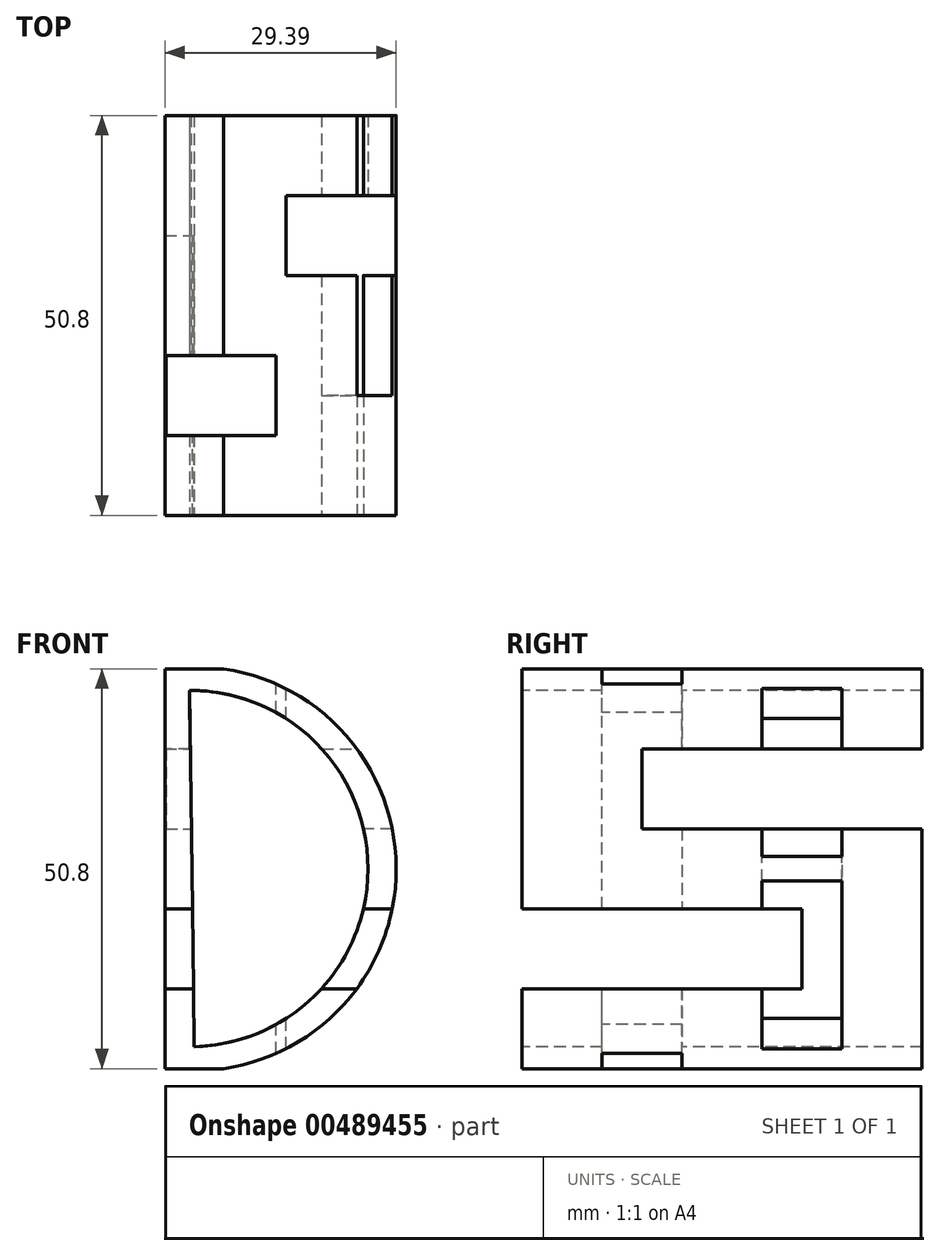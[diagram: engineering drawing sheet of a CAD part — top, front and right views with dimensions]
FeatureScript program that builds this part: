
annotation { "Feature Type Name" : "Feature", "Feature Type Description" : "" }
export const myFeature = defineFeature(function(context is Context, id is Id, definition is map)
    precondition{}
    {
        {
            var Q0;
            Q0=qCreatedBy(makeId("Front.planeOp"),FACE);
            var sketch = newSketch(context, id + "F0", { "sketchPlane" : qUnion([Q0])});
            skLineSegment(sketch, "E0", {"start": v(0, 0) * mm, "end": v(0, 50.8) * mm});
            skLineSegment(sketch, "E1", {"start": v(0, 50.8) * mm, "end": v(50.8, 50.8) * mm});
            skLineSegment(sketch, "E2", {"start": v(50.8, 50.8) * mm, "end": v(50.8, 0) * mm});
            skLineSegment(sketch, "E3", {"start": v(50.8, 0) * mm, "end": v(0, 0) * mm});
            skSolve(sketch);
        }
        {
            var Q0;
            Q0=makeQuery(id+"F0.imprint","IMPRINT",FACE,{"disambiguationData":[TD([[makeQuery(id+"F0.imprint","IMPRINT",EDGE,{"derivedFrom":sQuery(id+"F0.wireOp",EDGE,"E0")}),-1.0]])]});
            extrude(context, id + "F1", {"entities" : qUnion([Q0]), "depth" : 50.8 * mm, "offsetDistance" : 25.4 * mm});
        }
        {
            var Q0;
            Q0=qCreatedBy(makeId("Right.planeOp"),FACE);
            cPlane(context, id + "F2", {"entities" : qUnion([Q0]), "cplaneType" : CPlaneType.OFFSET, "offset" : 50.8 * mm, "width" : 152.4 * mm, "height" : 152.4 * mm});
        }
        {
            var Q0;
            Q0=qCreatedBy(makeId("Top.planeOp"),FACE);
            cPlane(context, id + "F3", {"entities" : qUnion([Q0]), "cplaneType" : CPlaneType.OFFSET, "offset" : 50.8 * mm, "width" : 152.4 * mm, "height" : 152.4 * mm});
        }
        {
            var Q0;
            Q0=makeQuery(id+"F1.opExtrude","CAP_FACE",FACE,{"disambiguationData":[OSD([sQuery(id+"F0.wireOp",EDGE,"E0"),sQuery(id+"F0.wireOp",EDGE,"E1"),sQuery(id+"F0.wireOp",EDGE,"E2"),sQuery(id+"F0.wireOp",EDGE,"E3")])],"isStart":false});
            var sketch = newSketch(context, id + "F4", { "sketchPlane" : qUnion([Q0])});
            skLineSegment(sketch, "E4", {"start": v(0, 50.8) * mm, "end": v(0, 0) * mm});
            skLineSegment(sketch, "E5", {"start": v(0, 0) * mm, "end": v(13.76, 0) * mm});
            skLineSegment(sketch, "E6", {"start": v(20.32, 50.8) * mm, "end": v(20.32, 0) * mm});
            skLineSegment(sketch, "E7", {"start": v(20.32, 0) * mm, "end": v(13.76, 0) * mm});
            skLineSegment(sketch, "E8", {"start": v(20.32, 50.8) * mm, "end": v(0, 50.8) * mm});
            skArc(sketch, "E9", {"start": v(20.32, 0) * mm, "mid": v(49.71, 25.4) * mm, "end": v(20.32, 50.8) * mm});
            skLineSegment(sketch, "E10", {"start": v(23.44, 48.05) * mm, "end": v(24.04, 2.8) * mm});
            skArc(sketch, "E11", {"start": v(24.04, 2.8) * mm, "mid": v(46.12, 25.72) * mm, "end": v(23.44, 48.05) * mm});
            skSolve(sketch);
        }
        {
            var Q0;
            Q0=makeQuery(id+"F4.imprint","IMPRINT",FACE,{"disambiguationData":[TD([[makeQuery(id+"F4.imprint","IMPRINT",EDGE,{"derivedFrom":sQuery(id+"F4.wireOp",EDGE,"E4")}),-1.0]])]});
            var Q1;
            Q1=makeQuery(id+"F4.imprint","IMPRINT",FACE,{"disambiguationData":[TD([[makeQuery(id+"F4.imprint","IMPRINT",EDGE,{"derivedFrom":sQuery(id+"F4.wireOp",EDGE,"E10")}),1.0]])]});
            var Q2;
            {var subQ5=makeQuery(id+"F1.opExtrude","CAP_EDGE",EDGE,{"disambiguationData":[OSD([sQuery(id+"F0.wireOp",EDGE,"E2")])],"isStart":false});Q2=makeQuery(id+"F4.imprint","IMPRINT",FACE,{"disambiguationData":[TD([[makeQuery(id+"F4.imprint","IMPRINT",EDGE,{"derivedFrom":subQ5}),-1.0]])]});}
            extrude(context, id + "F5", {"entities" : qUnion([Q0, Q1, Q2]), "operationType" : NewBodyOperationType.REMOVE, "oppositeDirection" : true, "depth" : 50.8 * mm, "offsetDistance" : 25.4 * mm});
        }
        {
            var Q0;
            Q0=qCreatedBy(id+"F2.planeOp",FACE);
            var sketch = newSketch(context, id + "F6", { "sketchPlane" : qUnion([Q0])});
            skLineSegment(sketch, "E12", {"start": v(-50.8, 50.8) * mm, "end": v(-50.8, 0) * mm});
            skLineSegment(sketch, "E13", {"start": v(-50.8, 0) * mm, "end": v(0, 0) * mm});
            skLineSegment(sketch, "E14", {"start": v(0, 0) * mm, "end": v(0, 50.8) * mm});
            skLineSegment(sketch, "E15", {"start": v(0, 50.8) * mm, "end": v(-50.8, 50.8) * mm});
            skLineSegment(sketch, "E16", {"start": v(0, 40.64) * mm, "end": v(-35.56, 40.64) * mm});
            skLineSegment(sketch, "E17", {"start": v(-35.56, 40.64) * mm, "end": v(-35.56, 30.48) * mm});
            skLineSegment(sketch, "E18", {"start": v(-35.56, 30.48) * mm, "end": v(0, 30.48) * mm});
            skLineSegment(sketch, "E19", {"start": v(-50.8, 10.16) * mm, "end": v(-15.24, 10.16) * mm});
            skLineSegment(sketch, "E20", {"start": v(-15.24, 10.16) * mm, "end": v(-15.24, 20.32) * mm});
            skLineSegment(sketch, "E21", {"start": v(-15.24, 20.32) * mm, "end": v(-50.8, 20.32) * mm});
            skSolve(sketch);
        }
        {
            var Q0;
            {var subQ0=sQuery(id+"F6.wireOp",EDGE,"E16");Q0=makeQuery(id+"F6.imprint","IMPRINT",FACE,{"disambiguationData":[TD([[makeQuery(id+"F6.imprint","IMPRINT",EDGE,{"derivedFrom":subQ0}),1.0]])]});}
            var Q1;
            {var subQ0=sQuery(id+"F6.wireOp",EDGE,"E19");Q1=makeQuery(id+"F6.imprint","IMPRINT",FACE,{"disambiguationData":[TD([[makeQuery(id+"F6.imprint","IMPRINT",EDGE,{"derivedFrom":subQ0}),1.0]])]});}
            extrude(context, id + "F7", {"entities" : qUnion([Q0, Q1]), "operationType" : NewBodyOperationType.REMOVE, "oppositeDirection" : true, "depth" : 50.8 * mm, "offsetDistance" : 25.4 * mm});
        }
        {
            var Q0;
            Q0=qCreatedBy(id+"F3.planeOp",FACE);
            var sketch = newSketch(context, id + "F8", { "sketchPlane" : qUnion([Q0])});
            skLineSegment(sketch, "E22", {"start": v(20.45, 0) * mm, "end": v(20.45, -50.8) * mm});
            skLineSegment(sketch, "E23", {"start": v(20.45, -50.8) * mm, "end": v(49.66, -50.8) * mm});
            skLineSegment(sketch, "E24", {"start": v(49.66, -50.8) * mm, "end": v(49.66, 0) * mm});
            skLineSegment(sketch, "E25", {"start": v(49.66, 0) * mm, "end": v(20.45, 0) * mm});
            skLineSegment(sketch, "E26", {"start": v(49.66, -10.16) * mm, "end": v(35.7, -10.16) * mm});
            skLineSegment(sketch, "E27", {"start": v(35.7, -10.16) * mm, "end": v(35.7, -20.32) * mm});
            skLineSegment(sketch, "E28", {"start": v(35.7, -20.32) * mm, "end": v(49.66, -20.32) * mm});
            skLineSegment(sketch, "E29", {"start": v(20.45, -40.64) * mm, "end": v(34.42, -40.64) * mm});
            skLineSegment(sketch, "E30", {"start": v(34.42, -40.64) * mm, "end": v(34.42, -30.48) * mm});
            skLineSegment(sketch, "E31", {"start": v(34.42, -30.48) * mm, "end": v(20.45, -30.48) * mm});
            skSolve(sketch);
        }
        {
            var Q0;
            {var subQ0=sQuery(id+"F8.wireOp",EDGE,"E26");Q0=makeQuery(id+"F8.imprint","IMPRINT",FACE,{"disambiguationData":[TD([[makeQuery(id+"F8.imprint","IMPRINT",EDGE,{"derivedFrom":subQ0}),1.0]])]});}
            var Q1;
            {var subQ0=sQuery(id+"F8.wireOp",EDGE,"E29");Q1=makeQuery(id+"F8.imprint","IMPRINT",FACE,{"disambiguationData":[TD([[makeQuery(id+"F8.imprint","IMPRINT",EDGE,{"derivedFrom":subQ0}),1.0]])]});}
            extrude(context, id + "F9", {"entities" : qUnion([Q0, Q1]), "operationType" : NewBodyOperationType.REMOVE, "oppositeDirection" : true, "depth" : 50.8 * mm, "offsetDistance" : 25.4 * mm});
        }
    });
